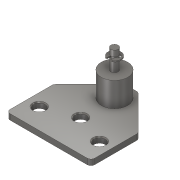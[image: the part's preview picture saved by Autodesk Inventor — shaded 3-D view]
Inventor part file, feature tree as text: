
AUTODESK INVENTOR PART (.ipt)
format: ipt  version: 2019.4 (Build 234330000, 330)  size: 167,936 bytes
history: native  units: in
note: dims shown in document units (in); Inventor stores cm internally (conversion verified against a paired STEP export)
features: fillet x2
ambient origin geometry x8: Origin, YZ Plane, XZ Plane, XY Plane, X Axis, Y Axis, Z Axis, Center Point
bodies: Solid1 (feature_tree), Solid2 (feature_tree)
feature tree (2):
  fillet  "Fillet2"  [1 undecoded]
  fillet  "Fillet3"  [1 undecoded]
note: 2 required parameter values undecoded (feature->parameter linkage not recoverable at this tier; creation-order binding heuristic only, values carry confidence <= 0.55)
